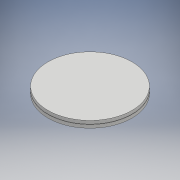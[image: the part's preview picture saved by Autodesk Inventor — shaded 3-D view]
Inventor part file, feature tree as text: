
AUTODESK INVENTOR PART (.ipt)
format: ipt  version: 2018 (Build 220112000, 112)  size: 97,792 bytes
history: native  units: mm
features: extrude x1, pattern_linear x1, sketch x1
ambient origin geometry x8: Origin, YZ Plane, XZ Plane, XY Plane, X Axis, Y Axis, Z Axis, Center Point
bodies: Solid1 (feature_tree)
feature tree (3):
  extrude  "Extrusion1"  Depth=1.9mm TaperAngle=0.0deg
  pattern_linear  "Rectangular Pattern1"  Count1=2 Spacing1=2.1mm
  sketch  "Sketch1"  dims[d0=50.0mm d1=1.9mm d2=0.0mm d3=20.0mm d5=2.1mm]
